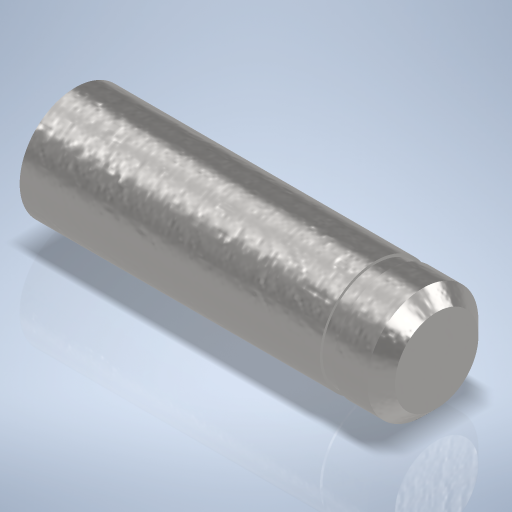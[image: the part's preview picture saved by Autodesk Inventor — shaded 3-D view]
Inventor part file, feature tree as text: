
AUTODESK INVENTOR PART (.ipt)
format: ipt  version: 2024 (Build 280153000, 153)  size: 323,072 bytes
history: native  units: mm
features: revolve x1, chamfer x1, sketch x1
ambient origin geometry x8: Origin, YZ Plane, XZ Plane, XY Plane, X Axis, Y Axis, Z Axis, Center Point
bodies: Volumenkörper1 (feature_tree)
feature tree (3):
  revolve  "Umdrehung1"
  chamfer  "Fasen1"  Distance=0.5mm
  sketch  "Skizze1"  dims[d0=13.0mm d1=0.5mm d2=10.8mm d4=3.8mm d5=4.0mm d6=360.0deg d7=0.5mm d8=2.0mm d9=45.0deg]
